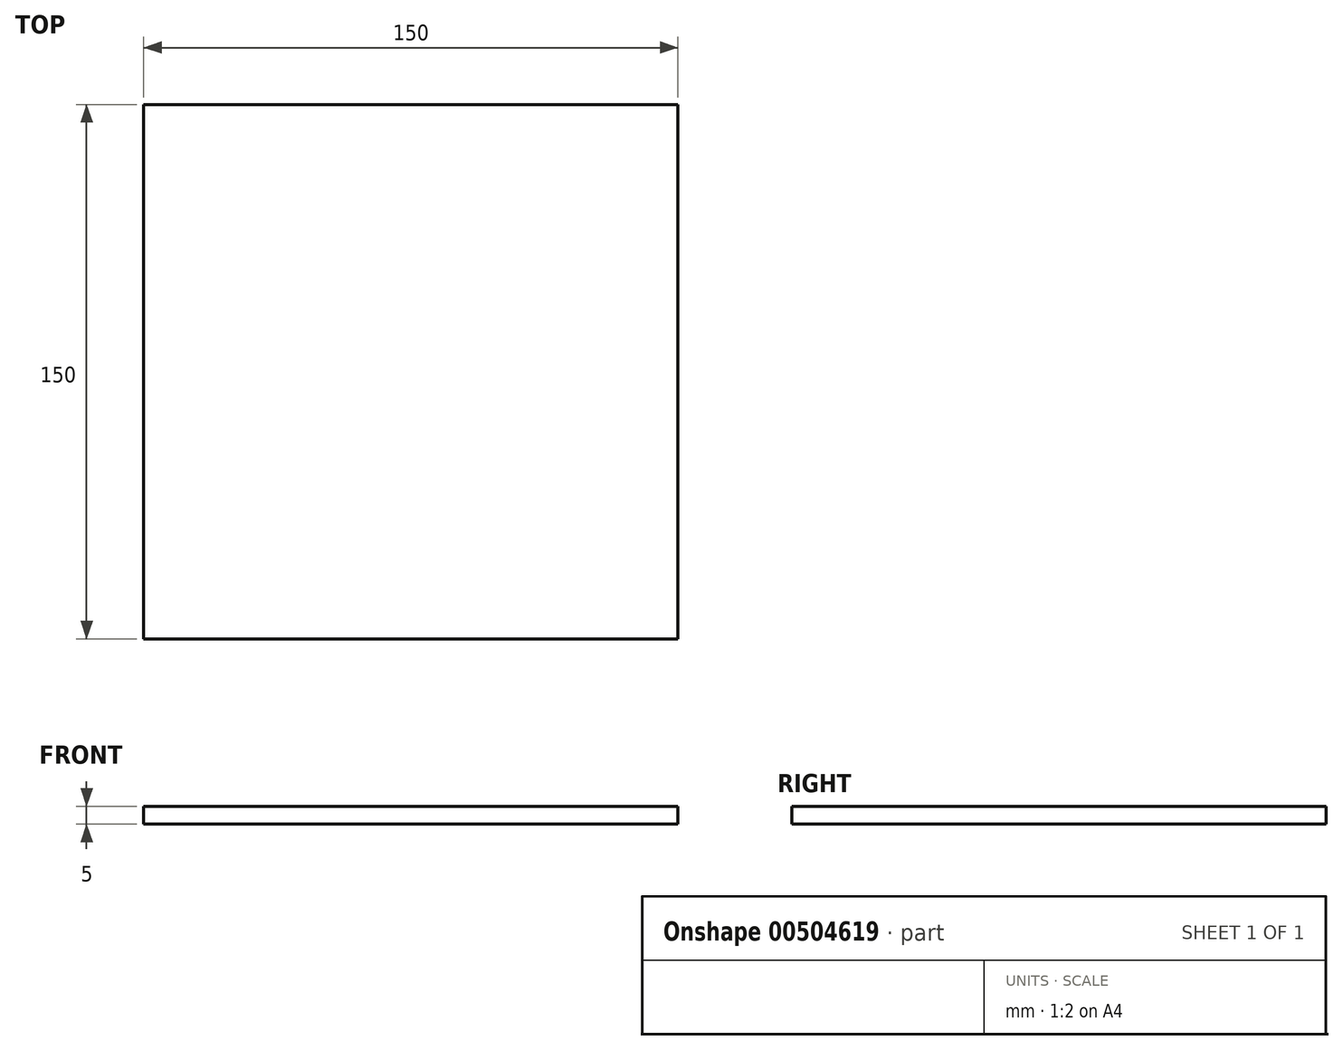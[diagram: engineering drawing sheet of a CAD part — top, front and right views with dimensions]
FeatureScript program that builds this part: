
annotation { "Feature Type Name" : "Feature", "Feature Type Description" : "" }
export const myFeature = defineFeature(function(context is Context, id is Id, definition is map)
    precondition{}
    {
        {
            var Q0;
            Q0=qCreatedBy(makeId("Top.planeOp"),FACE);
            var sketch = newSketch(context, id + "F0", { "sketchPlane" : qUnion([Q0])});
            skLineSegment(sketch, "E0.rect.bottom", {"start": v(75, 75) * mm, "end": v(-75, 75) * mm});
            skLineSegment(sketch, "E0.rect.top", {"start": v(75, -75) * mm, "end": v(-75, -75) * mm});
            skLineSegment(sketch, "E0.rect.left", {"start": v(75, 75) * mm, "end": v(75, -75) * mm});
            skLineSegment(sketch, "E0.rect.right", {"start": v(-75, 75) * mm, "end": v(-75, -75) * mm});
            skPoint(sketch, "E0.rect.middle", {"position": v(0, 0) * mm});
            skSolve(sketch);
        }
        {
            var Q0;
            Q0=qSketchRegion(id+"F0",true);
            extrude(context, id + "F1", {"entities" : qUnion([Q0]), "depth" : 5 * mm, "offsetDistance" : 25 * mm});
        }
    });
